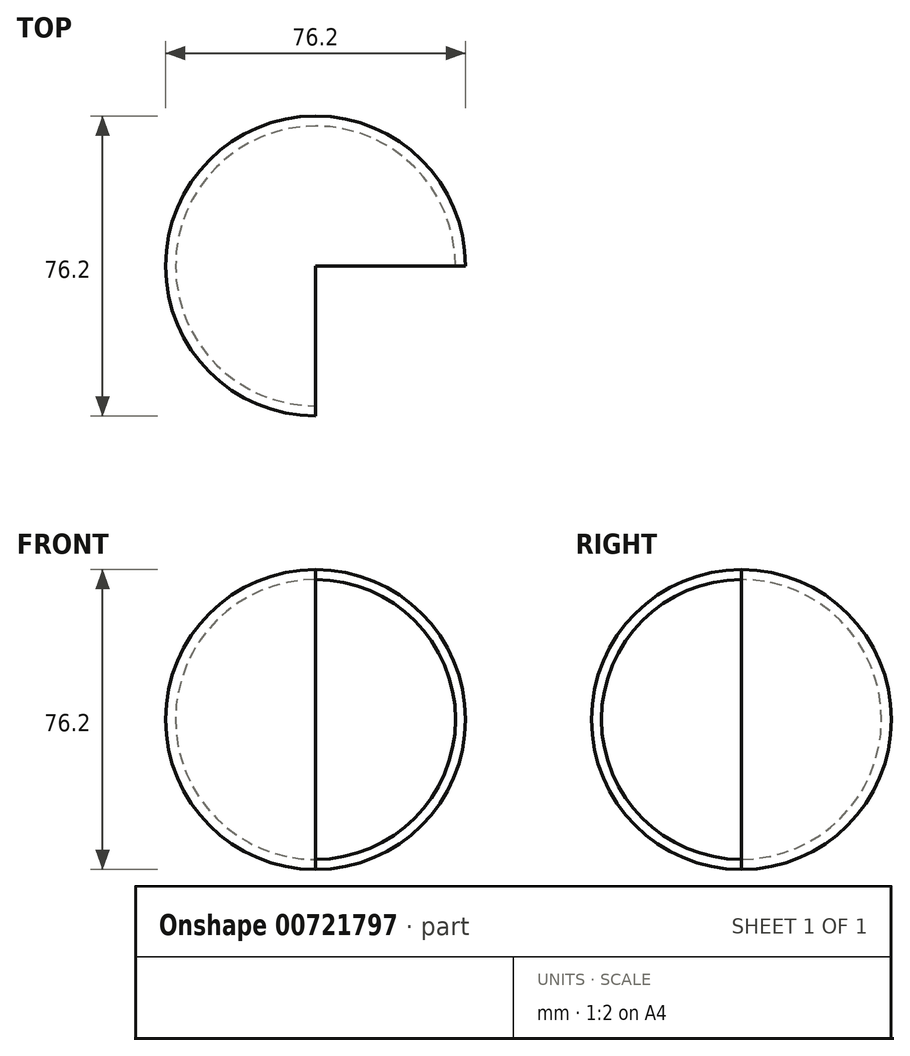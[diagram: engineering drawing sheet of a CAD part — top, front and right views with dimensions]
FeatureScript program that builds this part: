
annotation { "Feature Type Name" : "Feature", "Feature Type Description" : "" }
export const myFeature = defineFeature(function(context is Context, id is Id, definition is map)
    precondition{}
    {
        {
            var Q0;
            Q0=qCreatedBy(makeId("Front.planeOp"),FACE);
            var sketch = newSketch(context, id + "F0", { "sketchPlane" : qUnion([Q0])});
            skLineSegment(sketch, "E0", {"start": v(0, -38.1) * mm, "end": v(0, 38.1) * mm, "construction": true});
            skArc(sketch, "E1", {"start": v(0, -38.1) * mm, "mid": v(38.1, 0) * mm, "end": v(0, 38.1) * mm});
            skArc(sketch, "E2.0", {"start": v(0, -35.56) * mm, "mid": v(35.56, 0) * mm, "end": v(0, 35.56) * mm});
            skLineSegment(sketch, "E3", {"start": v(0, 38.1) * mm, "end": v(0, 35.56) * mm});
            skLineSegment(sketch, "E4", {"start": v(0, -35.56) * mm, "end": v(0, -38.1) * mm});
            skSolve(sketch);
        }
        {
            var Q0;
            Q0=makeQuery(id+"F0.imprint","IMPRINT",FACE,{"disambiguationData":[TD([[makeQuery(id+"F0.imprint","IMPRINT",EDGE,{"derivedFrom":sQuery(id+"F0.wireOp",EDGE,"E1")}),1.0]])]});
            var Q1;
            Q1=sQuery(id+"F0.wireOp",EDGE,"E0");
            revolve(context, id + "F1", {"surfaceOperationType" : NewSurfaceOperationType.NEW, "entities" : qUnion([Q0]), "axis" : qUnion([Q1]), "revolveType" : RevolveType.ONE_DIRECTION, "angle" : 270 * degree});
        }
    });
